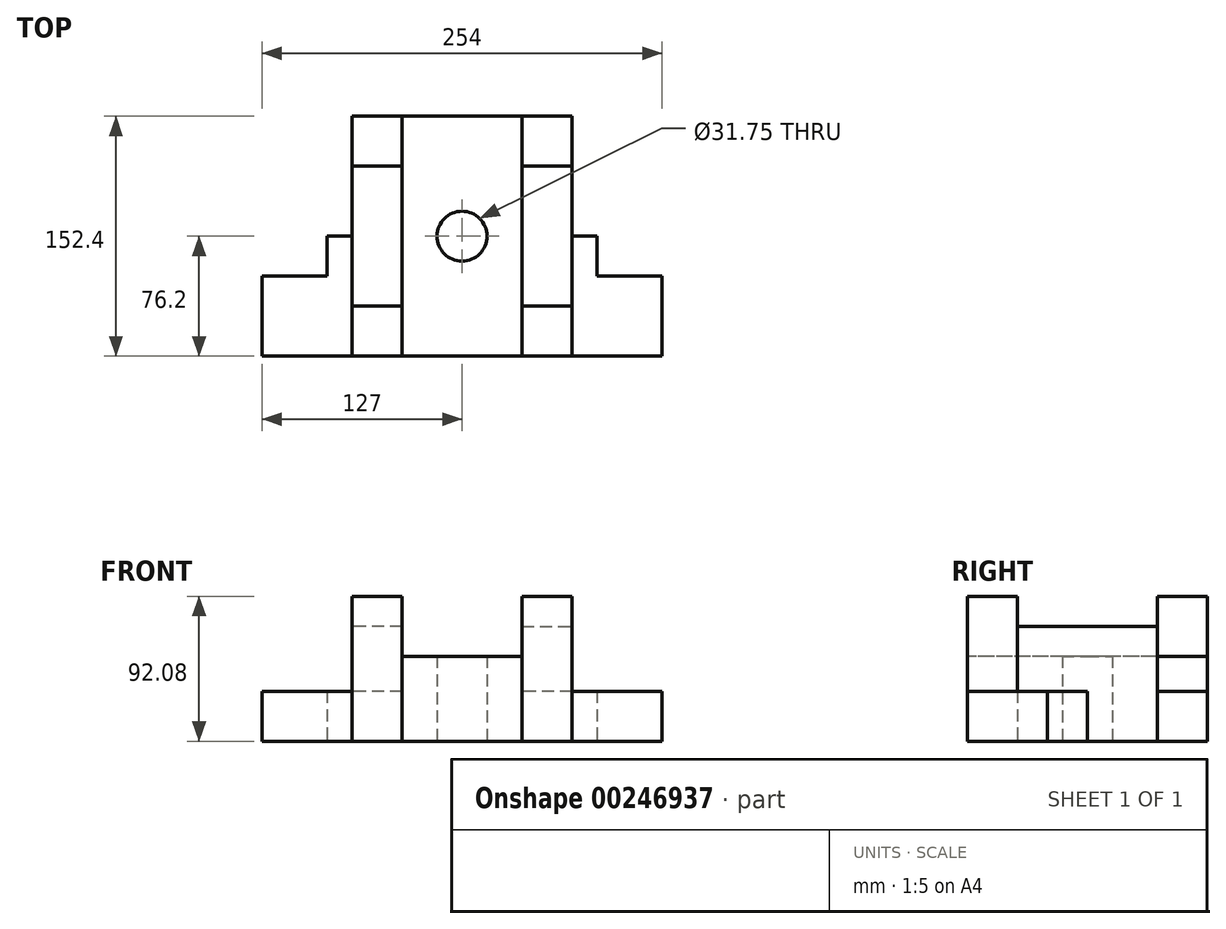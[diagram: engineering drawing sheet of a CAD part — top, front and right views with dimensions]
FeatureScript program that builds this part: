
annotation { "Feature Type Name" : "Feature", "Feature Type Description" : "" }
export const myFeature = defineFeature(function(context is Context, id is Id, definition is map)
    precondition{}
    {
        {
            var Q0;
            Q0=qCreatedBy(makeId("Top.planeOp"),FACE);
            var sketch = newSketch(context, id + "F0", { "sketchPlane" : qUnion([Q0])});
            skLineSegment(sketch, "E0.bottom", {"start": v(127, -76.2) * mm, "end": v(-127, -76.2) * mm});
            skLineSegment(sketch, "E0.top", {"start": v(127, 76.2) * mm, "end": v(-127, 76.2) * mm});
            skLineSegment(sketch, "E0.left", {"start": v(127, -76.2) * mm, "end": v(127, 76.2) * mm});
            skLineSegment(sketch, "E0.right", {"start": v(-127, -76.2) * mm, "end": v(-127, 76.2) * mm});
            skPoint(sketch, "E0.middle", {"position": v(0, 0) * mm});
            skLineSegment(sketch, "E1", {"start": v(127, 76.2) * mm, "end": v(127, 25.4) * mm});
            skLineSegment(sketch, "E2", {"start": v(127, 25.4) * mm, "end": v(85.72, 25.4) * mm});
            skLineSegment(sketch, "E3", {"start": v(85.72, 25.4) * mm, "end": v(85.72, -25.4) * mm});
            skLineSegment(sketch, "E4", {"start": v(85.72, -25.4) * mm, "end": v(127, -25.4) * mm});
            skLineSegment(sketch, "E5", {"start": v(0, 74.05) * mm, "end": v(0, -76.2) * mm});
            skPoint(sketch, "E5.startSnap0", {"position": v(0, 76.2) * mm});
            skLineSegment(sketch, "E6.MirrorCS", {"start": v(-127, 25.4) * mm, "end": v(-85.72, 25.4) * mm});
            skLineSegment(sketch, "E7.MirrorCS", {"start": v(-85.72, 25.4) * mm, "end": v(-85.72, -25.4) * mm});
            skLineSegment(sketch, "E8.MirrorCS", {"start": v(-85.72, -25.4) * mm, "end": v(-127, -25.4) * mm});
            skCircle(sketch, "E9", {"center": v(0, 0) * mm, "radius": 15.88 * mm});
            skLineSegment(sketch, "E10", {"start": v(127, 76.2) * mm, "end": v(76.88, 76.2) * mm});
            skLineSegment(sketch, "E11", {"start": v(76.88, 76.2) * mm, "end": v(127, 76.2) * mm});
            skLineSegment(sketch, "E12", {"start": v(69.85, 76.2) * mm, "end": v(127, 76.2) * mm});
            skLineSegment(sketch, "E13", {"start": v(69.85, 76.2) * mm, "end": v(69.85, -76.2) * mm});
            skLineSegment(sketch, "E14.MirrorCS", {"start": v(-69.85, 76.2) * mm, "end": v(-69.85, -76.2) * mm});
            skLineSegment(sketch, "E15", {"start": v(69.85, 76.2) * mm, "end": v(38.1, 76.2) * mm});
            skLineSegment(sketch, "E16", {"start": v(38.1, 76.2) * mm, "end": v(38.1, 44.45) * mm});
            skLineSegment(sketch, "E17.MirrorCS", {"start": v(-38.1, 76.2) * mm, "end": v(-38.1, 44.45) * mm});
            skLineSegment(sketch, "E18.MirrorCS", {"start": v(-69.85, 76.2) * mm, "end": v(-38.1, 76.2) * mm});
            skLineSegment(sketch, "E19", {"start": v(38.1, 44.45) * mm, "end": v(69.85, 44.45) * mm});
            skLineSegment(sketch, "E20", {"start": v(-127, 0) * mm, "end": v(127, 0) * mm});
            skLineSegment(sketch, "E21.MirrorCS", {"start": v(38.1, -44.45) * mm, "end": v(69.85, -44.45) * mm});
            skLineSegment(sketch, "E22.MirrorCS", {"start": v(38.1, -76.2) * mm, "end": v(38.1, -44.45) * mm});
            skLineSegment(sketch, "E23.MirrorCS", {"start": v(-38.1, -76.2) * mm, "end": v(-38.1, -44.45) * mm});
            skLineSegment(sketch, "E24", {"start": v(-38.1, 44.45) * mm, "end": v(-69.85, 44.45) * mm});
            skLineSegment(sketch, "E25.MirrorCS", {"start": v(-38.1, -44.45) * mm, "end": v(-69.85, -44.45) * mm});
            skLineSegment(sketch, "E26", {"start": v(-38.1, 76.2) * mm, "end": v(38.1, 76.2) * mm});
            skLineSegment(sketch, "E27", {"start": v(38.1, 44.45) * mm, "end": v(38.1, -44.45) * mm});
            skLineSegment(sketch, "E28", {"start": v(-38.1, 44.45) * mm, "end": v(-38.1, -44.45) * mm});
            skSolve(sketch);
        }
        {
            var Q0;
            {var subQ5=sQuery(id+"F0.wireOp",EDGE,"E1");Q0=makeQuery(id+"F0.imprint","IMPRINT",FACE,{"disambiguationData":[TD([[makeQuery(id+"F0.imprint","IMPRINT",EDGE,{"derivedFrom":subQ5}),-1.0]])]});}
            var Q1;
            {var subQ3=sQuery(id+"F0.wireOp",EDGE,"E4");Q1=makeQuery(id+"F0.imprint","IMPRINT",FACE,{"disambiguationData":[TD([[makeQuery(id+"F0.imprint","IMPRINT",EDGE,{"derivedFrom":subQ3}),-1.0]])]});}
            extrude(context, id + "F1", {"entities" : qUnion([Q0, Q1]), "depth" : 31.75 * mm});
        }
        {
            var Q0;
            {var subQ5=sQuery(id+"F0.wireOp",EDGE,"E0.top");Q0=makeQuery(id+"F0.imprint","IMPRINT",FACE,{"disambiguationData":[TD([[makeQuery(id+"F0.imprint","IMPRINT",EDGE,{"derivedFrom":subQ5}),1.0]])]});}
            var Q1;
            {var subQ0=sQuery(id+"F0.wireOp",EDGE,"E8.MirrorCS");Q1=makeQuery(id+"F0.imprint","IMPRINT",FACE,{"disambiguationData":[TD([[makeQuery(id+"F0.imprint","IMPRINT",EDGE,{"derivedFrom":subQ0}),1.0]])]});}
            extrude(context, id + "F2", {"entities" : qUnion([Q0, Q1]), "depth" : 31.75 * mm});
        }
        {
            var Q0;
            {var subQ4=sQuery(id+"F0.wireOp",EDGE,"E21.MirrorCS");Q0=makeQuery(id+"F0.imprint","IMPRINT",FACE,{"disambiguationData":[TD([[makeQuery(id+"F0.imprint","IMPRINT",EDGE,{"derivedFrom":subQ4}),-1.0]])]});}
            extrude(context, id + "F3", {"entities" : qUnion([Q0]), "depth" : 92.07 * mm});
        }
        {
            var Q0;
            Q0=makeQuery(id+"F0.imprint","IMPRINT",FACE,{"disambiguationData":[TD([[makeQuery(id+"F0.imprint","IMPRINT",EDGE,{"derivedFrom":sQuery(id+"F0.wireOp",EDGE,"E17.MirrorCS")}),-1.0]])]});
            var Q1;
            {var subQ3=sQuery(id+"F0.wireOp",EDGE,"E23.MirrorCS");Q1=makeQuery(id+"F0.imprint","IMPRINT",FACE,{"disambiguationData":[TD([[makeQuery(id+"F0.imprint","IMPRINT",EDGE,{"derivedFrom":subQ3}),1.0]])]});}
            var Q2;
            {var subQ0=sQuery(id+"F0.wireOp",EDGE,"E15");Q2=makeQuery(id+"F0.imprint","IMPRINT",FACE,{"disambiguationData":[TD([[makeQuery(id+"F0.imprint","IMPRINT",EDGE,{"derivedFrom":subQ0}),1.0]])]});}
            extrude(context, id + "F4", {"entities" : qUnion([Q0, Q1, Q2]), "depth" : 92.07 * mm});
        }
        {
            var Q0;
            {var subQ5=sQuery(id+"F0.wireOp",EDGE,"E16");Q0=makeQuery(id+"F0.imprint","IMPRINT",FACE,{"disambiguationData":[TD([[makeQuery(id+"F0.imprint","IMPRINT",EDGE,{"derivedFrom":subQ5}),-1.0]])]});}
            var Q1;
            {var subQ9=sQuery(id+"F0.wireOp",EDGE,"E23.MirrorCS");Q1=makeQuery(id+"F0.imprint","IMPRINT",FACE,{"disambiguationData":[TD([[makeQuery(id+"F0.imprint","IMPRINT",EDGE,{"derivedFrom":subQ9}),-1.0]])]});}
            var Q2;
            {var subQ7=sQuery(id+"F0.wireOp",EDGE,"E22.MirrorCS");Q2=makeQuery(id+"F0.imprint","IMPRINT",FACE,{"disambiguationData":[TD([[makeQuery(id+"F0.imprint","IMPRINT",EDGE,{"derivedFrom":subQ7}),1.0]])]});}
            extrude(context, id + "F5", {"entities" : qUnion([Q0, Q1, Q2]), "depth" : 53.97 * mm});
        }
        {
            var Q0;
            {var subQ0=sQuery(id+"F0.wireOp",EDGE,"E25.MirrorCS");Q0=makeQuery(id+"F0.imprint","IMPRINT",FACE,{"disambiguationData":[TD([[makeQuery(id+"F0.imprint","IMPRINT",EDGE,{"derivedFrom":subQ0}),-1.0]])]});}
            var Q1;
            {var subQ0=sQuery(id+"F0.wireOp",EDGE,"E24");Q1=makeQuery(id+"F0.imprint","IMPRINT",FACE,{"disambiguationData":[TD([[makeQuery(id+"F0.imprint","IMPRINT",EDGE,{"derivedFrom":subQ0}),1.0]])]});}
            var Q2;
            {var subQ0=sQuery(id+"F0.wireOp",EDGE,"E19");Q2=makeQuery(id+"F0.imprint","IMPRINT",FACE,{"disambiguationData":[TD([[makeQuery(id+"F0.imprint","IMPRINT",EDGE,{"derivedFrom":subQ0}),-1.0]])]});}
            var Q3;
            {var subQ0=sQuery(id+"F0.wireOp",EDGE,"E21.MirrorCS");Q3=makeQuery(id+"F0.imprint","IMPRINT",FACE,{"disambiguationData":[TD([[makeQuery(id+"F0.imprint","IMPRINT",EDGE,{"derivedFrom":subQ0}),1.0]])]});}
            extrude(context, id + "F6", {"entities" : qUnion([Q0, Q1, Q2, Q3]), "depth" : 73.02 * mm});
        }
    });
